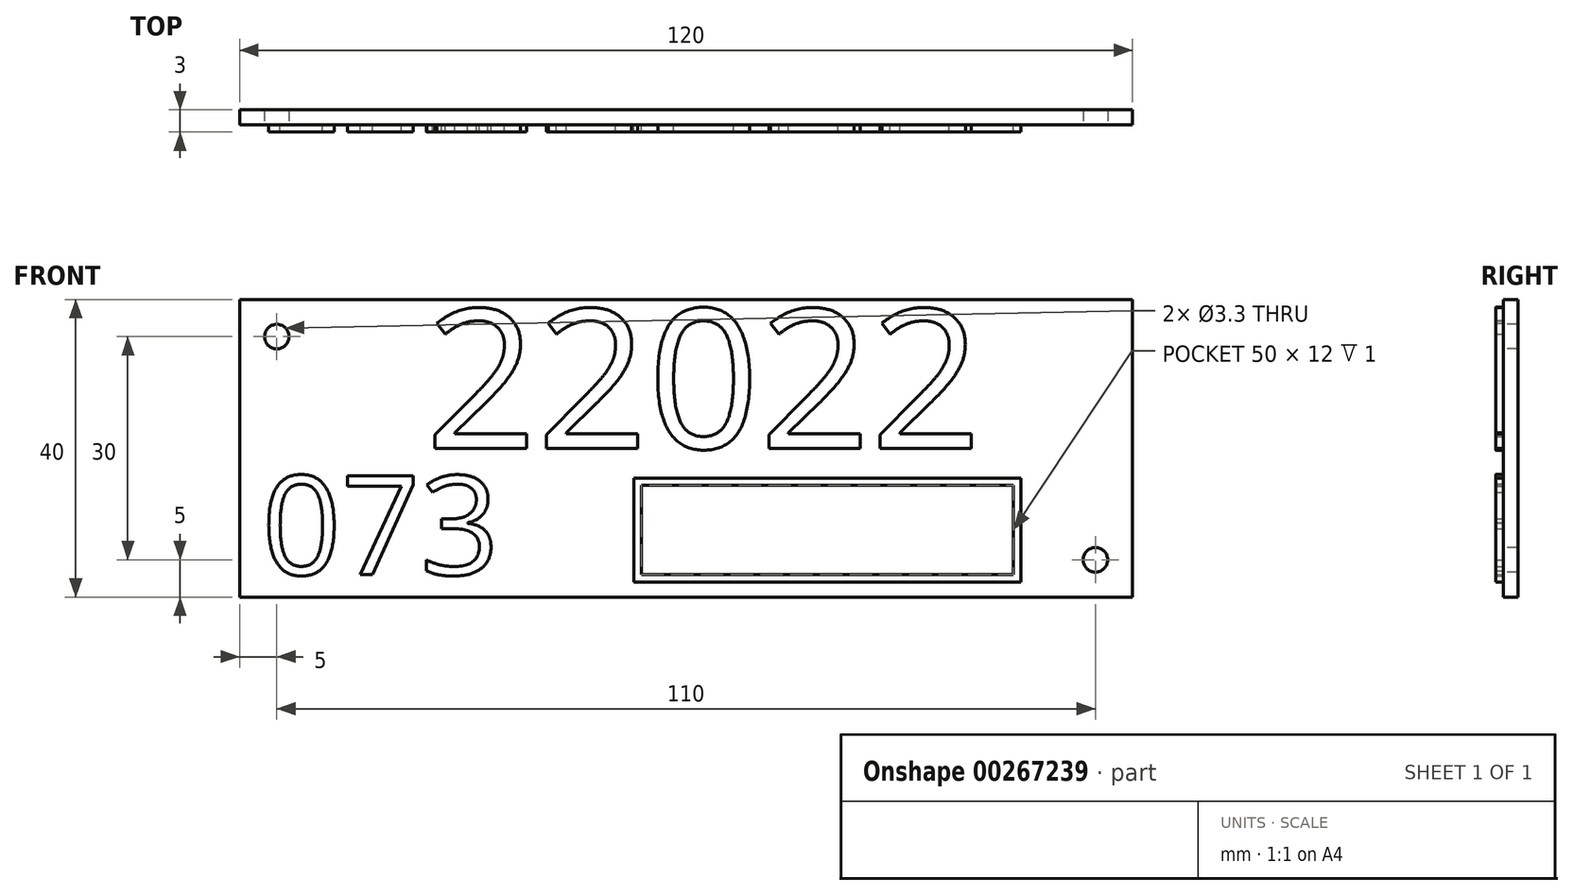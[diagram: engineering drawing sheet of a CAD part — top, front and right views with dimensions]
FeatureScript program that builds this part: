
annotation { "Feature Type Name" : "Feature", "Feature Type Description" : "" }
export const myFeature = defineFeature(function(context is Context, id is Id, definition is map)
    precondition{}
    {
        {
            var Q0;
            Q0=qCreatedBy(makeId("Front.planeOp"),FACE);
            var sketch = newSketch(context, id + "F0", { "sketchPlane" : qUnion([Q0])});
            skLineSegment(sketch, "E0.bottom", {"start": v(60, -20) * mm, "end": v(-60, -20) * mm});
            skLineSegment(sketch, "E0.top", {"start": v(60, 20) * mm, "end": v(-60, 20) * mm});
            skLineSegment(sketch, "E0.left", {"start": v(60, -20) * mm, "end": v(60, 20) * mm});
            skLineSegment(sketch, "E0.right", {"start": v(-60, -20) * mm, "end": v(-60, 20) * mm});
            skPoint(sketch, "E0.middle", {"position": v(0, 0) * mm});
            skSolve(sketch);
        }
        {
            var Q0;
            Q0=makeQuery(id+"F0.imprint","IMPRINT",FACE,{"disambiguationData":[TD([[makeQuery(id+"F0.imprint","IMPRINT",EDGE,{"derivedFrom":sQuery(id+"F0.wireOp",EDGE,"E0.bottom")}),-1.0]])]});
            extrude(context, id + "F1", {"entities" : qUnion([Q0]), "depth" : 2 * mm});
        }
        {
            var Q0;
            Q0=makeQuery(id+"F1.opExtrude","CAP_FACE",FACE,{"disambiguationData":[OSD([sQuery(id+"F0.wireOp",EDGE,"E0.bottom"),sQuery(id+"F0.wireOp",EDGE,"E0.top"),sQuery(id+"F0.wireOp",EDGE,"E0.left"),sQuery(id+"F0.wireOp",EDGE,"E0.right")])],"isStart":false});
            var sketch = newSketch(context, id + "F2", { "sketchPlane" : qUnion([Q0])});
            skPoint(sketch, "E1", {"position": v(-55, 15) * mm});
            skPoint(sketch, "E2", {"position": v(55, -15) * mm});
            skSolve(sketch);
        }
        {
            var Q0;
            Q0=sQuery(id+"F2.wireOp",VERTEX,"E1");
            var Q1;
            Q1=sQuery(id+"F2.wireOp",VERTEX,"E2");
            var Q2;
            Q2=makeQuery(id+"F1.opExtrude","SWEPT_BODY",BODY,{"disambiguationData":[OSD([sQuery(id+"F0.wireOp",EDGE,"E0.bottom"),sQuery(id+"F0.wireOp",EDGE,"E0.top"),sQuery(id+"F0.wireOp",EDGE,"E0.left"),sQuery(id+"F0.wireOp",EDGE,"E0.right")])]});
            hole(context, id + "F3", {"style" : HoleStyle.SIMPLE, "endStyle" : HoleEndStyle.THROUGH, "holeDiameter" : 3.3 * mm, "locations" : qUnion([Q0, Q1]), "scope" : qUnion([Q2]), "isTappedThrough" : true});
        }
        {
            var Q0;
            Q0=makeQuery(id+"F1.opExtrude","CAP_FACE",FACE,{"disambiguationData":[OSD([sQuery(id+"F0.wireOp",EDGE,"E0.bottom"),sQuery(id+"F0.wireOp",EDGE,"E0.top"),sQuery(id+"F0.wireOp",EDGE,"E0.left"),sQuery(id+"F0.wireOp",EDGE,"E0.right")])],"isStart":false});
            var sketch = newSketch(context, id + "F4", { "sketchPlane" : qUnion([Q0])});
            skText(sketch, "E3", { "text": "22022", "fontName": "OpenSans-Regular.ttf"});
            const initialGuessF4  = {"E3": [-0.035, 0, 1, 0, 0.01882]};
            skSetInitialGuess(sketch, initialGuessF4);
            skSolve(sketch);
        }
        {
            var Q0;
            Q0=qSketchRegion(id+"F4",true);
            extrude(context, id + "F5", {"entities" : qUnion([Q0]), "operationType" : NewBodyOperationType.ADD, "depth" : 1 * mm});
        }
        {
            var Q0;
            {var subQ0=sQuery(id+"F0.wireOp",EDGE,"E0.top");var subQ1=sQuery(id+"F0.wireOp",EDGE,"E0.left");var subQ2=sQuery(id+"F0.wireOp",EDGE,"E0.right");var subQ3=sQuery(id+"F0.wireOp",EDGE,"E0.bottom");Q0=makeQuery(id+"F5.boolean.opBoolean","SPLIT",FACE,{"disambiguationData":[TD([makeQuery(id+"F1.opExtrude","SWEPT_FACE",FACE,{"disambiguationData":[OSD([subQ3])]})])],"derivedFrom":makeQuery(id+"F1.opExtrude","CAP_FACE",FACE,{"disambiguationData":[OSD([subQ3,subQ0,subQ1,subQ2])],"isStart":false})});}
            var sketch = newSketch(context, id + "F6", { "sketchPlane" : qUnion([Q0])});
            skText(sketch, "E4", { "text": "073", "fontName": "OpenSans-Regular.ttf"});
            const initialGuessF6  = {"E4": [-0.057, -0.017, 1, 0, 0.01338]};
            skSetInitialGuess(sketch, initialGuessF6);
            skSolve(sketch);
        }
        {
            var Q0;
            Q0=qSketchRegion(id+"F6",true);
            extrude(context, id + "F7", {"entities" : qUnion([Q0]), "operationType" : NewBodyOperationType.ADD, "depth" : 1 * mm});
        }
        {
            var Q0;
            {var subQ46=sQuery(id+"F0.wireOp",EDGE,"E0.top");var subQ48=sQuery(id+"F0.wireOp",EDGE,"E0.left");var subQ66=sQuery(id+"F0.wireOp",EDGE,"E0.right");var subQ76=sQuery(id+"F0.wireOp",EDGE,"E0.bottom");var subQ77=makeQuery(id+"F1.opExtrude","SWEPT_FACE",FACE,{"disambiguationData":[OSD([subQ76])]});Q0=makeQuery(id+"F7.boolean.opBoolean","SPLIT",FACE,{"disambiguationData":[TD([subQ77])],"derivedFrom":makeQuery(id+"F5.boolean.opBoolean","SPLIT",FACE,{"disambiguationData":[TD([subQ77])],"derivedFrom":makeQuery(id+"F1.opExtrude","CAP_FACE",FACE,{"disambiguationData":[OSD([subQ76,subQ46,subQ48,subQ66])],"isStart":false})})});}
            var sketch = newSketch(context, id + "F8", { "sketchPlane" : qUnion([Q0])});
            skLineSegment(sketch, "E5.bottom", {"start": v(45, -18) * mm, "end": v(-7, -18) * mm});
            skLineSegment(sketch, "E5.top", {"start": v(45, -4) * mm, "end": v(-7, -4) * mm});
            skLineSegment(sketch, "E5.left", {"start": v(45, -18) * mm, "end": v(45, -4) * mm});
            skLineSegment(sketch, "E5.right", {"start": v(-7, -18) * mm, "end": v(-7, -4) * mm});
            skPoint(sketch, "E5.middle", {"position": v(19, -11) * mm});
            skLineSegment(sketch, "E6.0", {"start": v(44, -5) * mm, "end": v(-6, -5) * mm});
            skLineSegment(sketch, "E6.1", {"start": v(44, -17) * mm, "end": v(44, -5) * mm});
            skLineSegment(sketch, "E6.2", {"start": v(44, -17) * mm, "end": v(-6, -17) * mm});
            skLineSegment(sketch, "E6.3", {"start": v(-6, -17) * mm, "end": v(-6, -5) * mm});
            skSolve(sketch);
        }
        {
            var Q0;
            Q0=makeQuery(id+"F8.imprint","IMPRINT",FACE,{"disambiguationData":[TD([[makeQuery(id+"F8.imprint","IMPRINT",EDGE,{"derivedFrom":sQuery(id+"F8.wireOp",EDGE,"E5.bottom")}),-1.0]])]});
            extrude(context, id + "F9", {"entities" : qUnion([Q0]), "operationType" : NewBodyOperationType.ADD, "depth" : 1 * mm});
        }
    });
